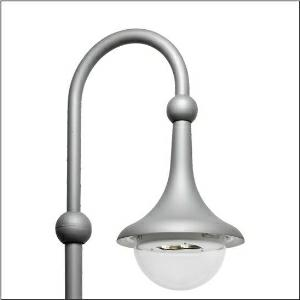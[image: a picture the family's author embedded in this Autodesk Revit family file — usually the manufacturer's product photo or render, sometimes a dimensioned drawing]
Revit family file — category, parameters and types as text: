
# Revit family: grosse_glocke_iq___st1_2a_5xa1565e1v108_00bb
name_source: partatom
category: Lighting Fixtures
units: mm (PartAtom-declared; Revit-internal decimal feet)

## family parameters
Cut with Voids When Loaded = No
Host = Face
Light Source = No
Part Type = Normal
Room Calculation Point = No
Round Connector Dimension = Use Diameter
Shared = No

## types (1)
- --- (1 x LED, 5180 lm, 34.3 W, 3000K)
    Apparent Load = 34 VA
    CIE Flux Codes = 28 66 95 100 100
    Color Rendering = 70
    Color Temperature = 3000K
    Default Elevation = 1800 mm
    Description = Large Bell iQ, mast luminaire, primary light control with 3 zone facetted reflector, of plastic, silver coated, primary optical cover: enclosure, of PMMA, transparent, light distribution: ST1.2a, light emission: direct distribution, primary light characteristic: asymmetric, installation type: suspended mounting, High Power LED, rated luminous flux: 5.180lm, luminous efficacy: 151lm/W, light colour: 730, colour temperature: 3000K, control gear: iQ-Street Remote, D4i with power reduction, control: optimised constant luminous flux control (CLO 2.0), Desk-Remote (wireless, voltage-free reading and setting of iQ features in the workshop via application-optimized NFC function/RFID function), Light-Fading, Smart-Wire, Night-Set, Lumen-Switch, Temp-Guard, Auto-Match, Street-Remote, pre-setting: logarithmic dimming characteristic, mains connection: 230..240V, AC, 50/60Hz, start of lifetime: 34W, end of service life: 38W, reduction: 16W, luminaire housing, bell-shaped, of glass-fibre reinforced polyester, coated, Siteco® metallic grey (DB 702S), please order curved mast extension separately, diameter: 530mm, height: 695mm, mounting height: 4..6m, Smart Interface above, protection rating (complete): IP54, insulation class (complete): insulation class II (safety insulation), certification: CE, ENEC, VDE, impact resistance: IK08, standard-compliant lighting for roads and squares, packaging unit: 1 piece

Light Distribution: ST1.2a
    Height = 695 mm
    Lamp = 1 x LED
    Lamp Light Flux = 5180 lm
    Lamp Power = 34.3 W
    Lamp count = 1
    Length = 530 mm
    Luminous efficacy = 151 lm/W
    Manufacturer = Siteco
    ModVariant = No
    Model = 5XA1565E1V108
    Number of Poles = 1
    OnlyDefault = Yes
    Power Factor = 1
    Product Name = Große Glocke iQ | ST1.2a
    Product group = mast luminaire | pylon annexe
    ProductGroupID = 6201
    Protection Class = Protection class II
    Protection Degree = IP 54
    RLX_Detail_Level = 1
    RLX_Emergency_Light_Flux = 0 lm
    RLX_Emergency_Type = 0
    RLX_Emergency_Type_DB = No
    RlxData = <blob elided: 85385 chars, md5=02f5034e>
    Socket = socket
    Standby Power = 0 W
    System Light Flux = 5180 lm
    System Power = 34 W
    Type Comments = factory setting: luminous flux: 100 % | dim-lin: 254 | 640 mA
    Type Image = l_1347688.jpg
    URL = http://relux.com
    VarID = @adj_059740
    Voltage = 0 V
    Weight = 0.00 kg
    Width = 0 mm  [stored 0 ft]

note: [stored X ft] marks values corroborated as IEEE doubles in the binary element streams (Revit-internal decimal feet)

## geometry (parser evidence)
native form markers: Blend x4, Sweep x11
no freeform markers — native parametric forms only
